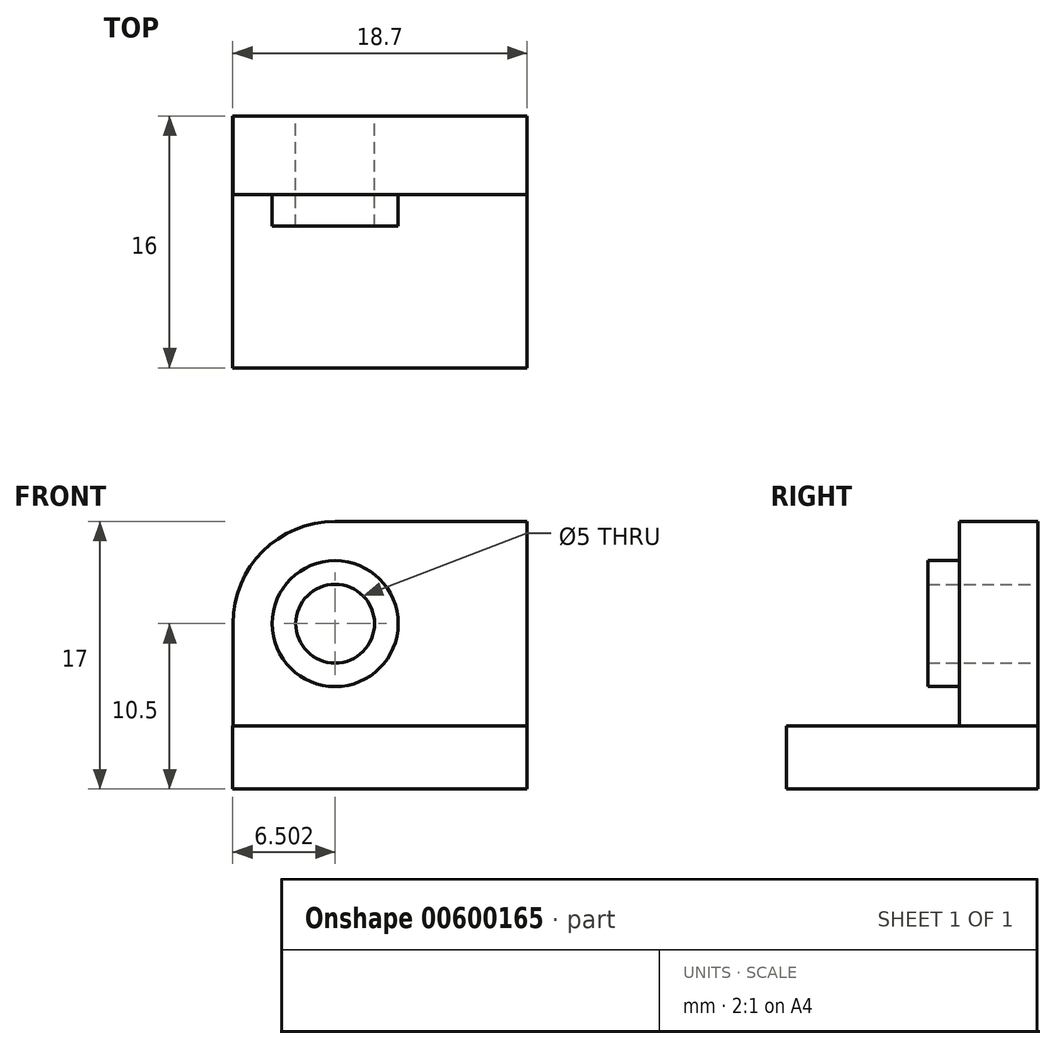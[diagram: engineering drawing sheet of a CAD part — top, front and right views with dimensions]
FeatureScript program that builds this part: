
annotation { "Feature Type Name" : "Feature", "Feature Type Description" : "" }
export const myFeature = defineFeature(function(context is Context, id is Id, definition is map)
    precondition{}
    {
        {
            var Q0;
            Q0=qCreatedBy(makeId("Front.planeOp"),FACE);
            var sketch = newSketch(context, id + "F0", { "sketchPlane" : qUnion([Q0])});
            skLineSegment(sketch, "E0.bottom", {"start": v(0, 0) * mm, "end": v(-12.2, 0) * mm});
            skLineSegment(sketch, "E0.top", {"start": v(0, 13) * mm, "end": v(-12.2, 13) * mm});
            skLineSegment(sketch, "E0.left", {"start": v(0, 0) * mm, "end": v(0, 13) * mm});
            skArc(sketch, "E1", {"start": v(-12.2, 13) * mm, "mid": v(-16.8, 11.1) * mm, "end": v(-18.7, 6.5) * mm});
            skPoint(sketch, "E2.end.orphan", {"position": v(-9, 0) * mm});
            skPoint(sketch, "E2.start.orphan", {"position": v(-9, 13) * mm});
            skPoint(sketch, "E3.orphan", {"position": v(-18, 13) * mm});
            skPoint(sketch, "E4.orphan", {"position": v(-18, 0) * mm});
            skCircle(sketch, "E5", {"center": v(-12.2, 6.5) * mm, "radius": 2.5 * mm});
            skLineSegment(sketch, "E6", {"start": v(-18.7, 6.5) * mm, "end": v(-18.7, 0) * mm});
            skLineSegment(sketch, "E7", {"start": v(-18.7, 0) * mm, "end": v(-12.2, 0) * mm});
            skSolve(sketch);
        }
        {
            var Q0;
            Q0 = qSketchRegion(id + "F0", true);
            extrude(context, id + "F1", {"entities" : qUnion([Q0]), "depth" : 5 * mm, "offsetDistance" : 25 * mm});
        }
        {
            var Q0;
            Q0=makeQuery(id+"F1.opExtrude","CAP_FACE",FACE,{"disambiguationData":[OSD([sQuery(id+"F0.wireOp",EDGE,"E0.bottom"),sQuery(id+"F0.wireOp",EDGE,"E0.top"),sQuery(id+"F0.wireOp",EDGE,"E0.left"),sQuery(id+"F0.wireOp",EDGE,"E1"),sQuery(id+"F0.wireOp",EDGE,"E5"),sQuery(id+"F0.wireOp",EDGE,"E6"),sQuery(id+"F0.wireOp",EDGE,"E7")])],"isStart":false});
            var sketch = newSketch(context, id + "F2", { "sketchPlane" : qUnion([Q0])});
            skCircle(sketch, "E8", {"center": v(-12.2, 6.5) * mm, "radius": 2.5 * mm});
            skCircle(sketch, "E9", {"center": v(-12.2, 6.5) * mm, "radius": 4 * mm});
            skSolve(sketch);
        }
        {
            var Q0;
            Q0 = qSketchRegion(id + "F2", true);
            extrude(context, id + "F3", {"entities" : qUnion([Q0]), "operationType" : NewBodyOperationType.ADD, "depth" : 2 * mm, "offsetDistance" : 25 * mm});
        }
        {
            var Q0;
            Q0=qCreatedBy(makeId("Top.planeOp"),FACE);
            var sketch = newSketch(context, id + "F4", { "sketchPlane" : qUnion([Q0])});
            skLineSegment(sketch, "E10.bottom", {"start": v(0, 0) * mm, "end": v(-18.7, 0) * mm});
            skLineSegment(sketch, "E10.top", {"start": v(0, -16) * mm, "end": v(-18.7, -16) * mm});
            skLineSegment(sketch, "E10.left", {"start": v(0, 0) * mm, "end": v(0, -16) * mm});
            skLineSegment(sketch, "E10.right", {"start": v(-18.7, 0) * mm, "end": v(-18.7, -16) * mm});
            skSolve(sketch);
        }
        {
            var Q0;
            Q0 = qSketchRegion(id + "F4", true);
            extrude(context, id + "F5", {"entities" : qUnion([Q0]), "oppositeDirection" : true, "depth" : 4 * mm, "offsetDistance" : 25 * mm});
        }
    });
